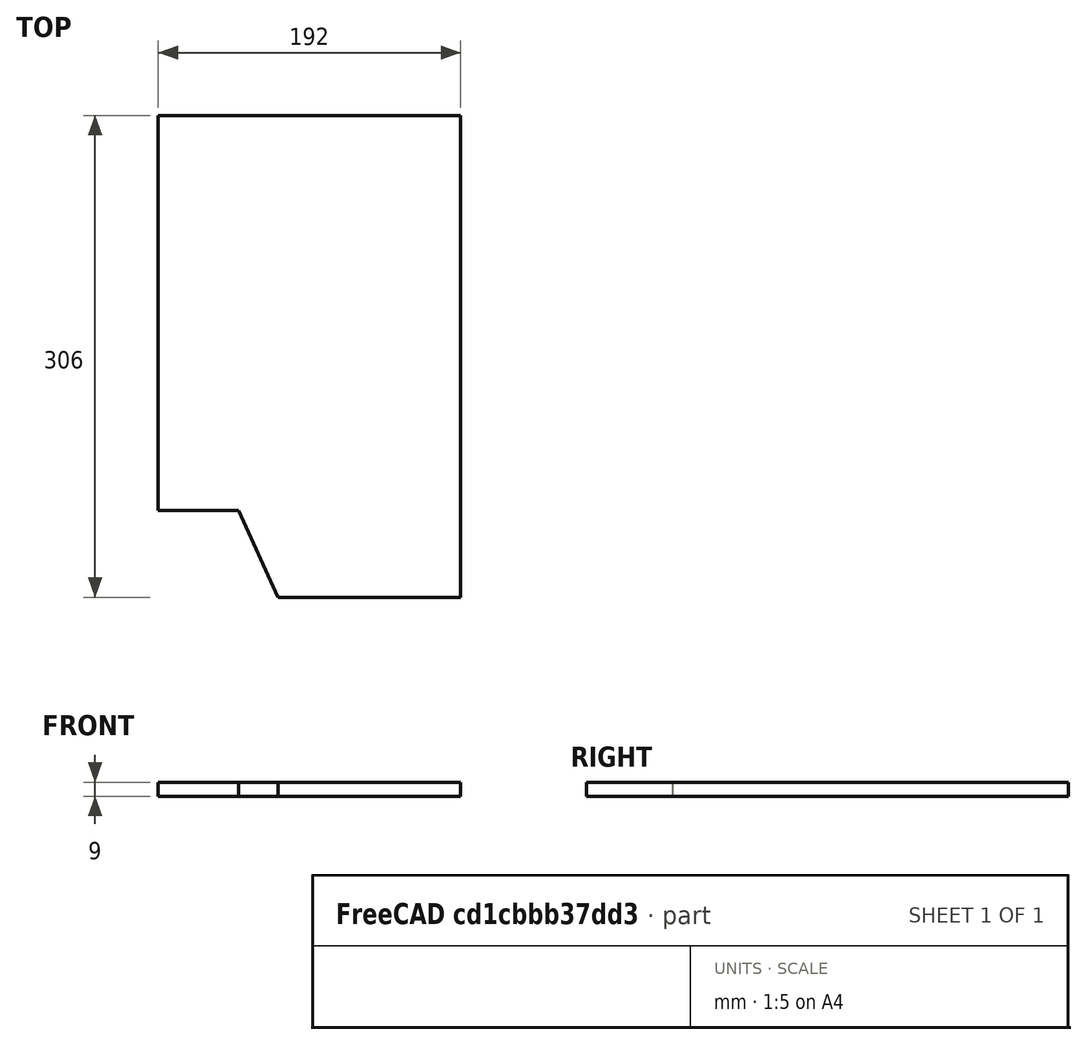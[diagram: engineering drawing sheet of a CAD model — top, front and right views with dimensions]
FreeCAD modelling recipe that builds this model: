
FCSTD DOCUMENT  (FreeCAD 0.16RUnknown)
Label: plaque_gd
License: All rights reserved
LicenseURL: http://en.wikipedia.org/wiki/All_rights_reserved
objects: App::FeaturePython×6, Drawing::FeatureViewPart×4, App::DocumentObjectGroup×4, Drawing::FeatureViewPython×3, Part::Plane×1, Part::Feature×1, Part::Cut×1, Part::FeaturePython×1, Part::Extrusion×1, Drawing::FeaturePage×1
note: 5 computed .brp shape members not serialized (recipe doc carries the construction recipe); baked Part::Feature solids carry a one-line shape summary decoded from their .brp

FEATURE [Part::Plane] square
  Length = 192
  Placement = pos=(9,20,0) rot=(0,0,1;0rad)
  Width = 306
FEATURE [Part::Feature] polygon
  shape: bbox 76 x 55 x 2e-07 mm, 1 faces, 0 solids (baked)
FEATURE [Part::Cut] difference
  Base = -> square
  Tool = -> polygon
FEATURE [Part::FeaturePython] RefineLinearExtrude  # WARN: FeaturePython — macro-defined, semantics opaque (R4)
  Base = -> difference
FEATURE [Part::Extrusion] LinearExtrude
  Base = -> RefineLinearExtrude
  Dir = (0,0,9)
  Solid = true
FEATURE [App::FeaturePython] Dimension001  # Draft dimension (typed FeaturePython)
  Dimline = (0,338,0)
  Direction = (0,0,0)
  Distance = 192
  End = (201,326,0)
  Normal = (0,0,1)
  Start = (9,326,0)
FEATURE [Drawing::FeatureViewPart] Ortho  label="Ortho_0_0"
  Direction = (1,0,0)
  HiddenWidth = 0.15
  LineWidth = 0.35
  Rotation = -90
  Scale = 0.38
  ShowHiddenLines = true
  ShowSmoothLines = false
  Source = -> LinearExtrude
  Tolerance = 0.05
  ViewResult = <g id="Ortho_0_0"\n   transform="rotate(-90,94.26,60.61) translate(94.26,60.61) scale(0.38,0.38)"\n  >\n<g   stroke="rgb(0, 0, 0)"\n   stroke-width="0.394737"\n   stroke-linecap="butt"\n   stroke-linejoin="miter"\n   stroke-dasharray="0.2,0.1"\n   fill="none"\n   transform="scale(1,-1)"\n  >\n<path id= "1" d=" M 0 -75 L 9 -75 " />\n<path id= "2" d=" M 0 -326 L 9 -326 " />\n<path id= "3" d=" M 0 -75 L 0 -326 " />\n<path id= "4" d=" M 9 -75 L 9 -326 " />\n<path id= "5" d=" M 0 -20 L 9 -20 " />\n<path id= "6" d=" M 0 -75 L 9 -75 " />\n<path id= "7" d=" M 0 -75 L 0 -20 " />\n<path id= "8" d=" M 9 -75 L 9 -20 " />\n</g>\n<g   stroke="rgb(0, 0, 0)"\n   stroke-width="0.921053"\n   stroke-linecap="butt"\n   stroke-linejoin="miter"\n   fill="none"\n   transform="scale(1,-1)"\n  >\n<path id= "1" d=" M 0 -326 L 9 -326 " />\n<path id= "2" d=" M 0 -20 L 9 -20 " />\n<path id= "3" d=" M 0 -20 L 0 -326 " />\n<path id= "4" d=" M 9 -20 L 9 -326 " />\n</g>\n</g>
  Visible = true
  X = 94.26
  Y = 60.61
FEATURE [Drawing::FeatureViewPart] Ortho001  label="Ortho_0_-1"
  Direction = (0,0,1)
  HiddenWidth = 0.15
  LineWidth = 0.35
  Rotation = 90
  Scale = 0.38
  ShowHiddenLines = false
  ShowSmoothLines = false
  Source = -> LinearExtrude
  Tolerance = 0.05
  ViewResult = <g id="Ortho_0_-1"\n   transform="rotate(90,94.26,103.89) translate(94.26,103.89) scale(0.38,0.38)"\n  >\n<g   stroke="rgb(0, 0, 0)"\n   stroke-width="0.921053"\n   stroke-linecap="butt"\n   stroke-linejoin="miter"\n   fill="none"\n   transform="scale(1,-1)"\n  >\n<path id= "1" d=" M 9 75 L 9 326 " />\n<path id= "2" d=" M 9 326 L 201 326 " />\n<path id= "3" d=" M 201 20 L 201 326 " />\n<path id= "4" d=" M 85 20 L 201 20 " />\n<path id= "5" d=" M 60 75 L 85 20 " />\n<path id= "6" d=" M 9 75 L 60 75 " />\n</g>\n</g>
  Visible = true
  X = 94.26
  Y = 103.89
FEATURE [Drawing::FeatureViewPart] Ortho002  label="Ortho_1_-1"
  Direction = (0.57735,-0.57735,0.57735)
  HiddenWidth = 0.15
  LineWidth = 0.35
  Rotation = 60
  Scale = 0.38
  ShowHiddenLines = false
  ShowSmoothLines = false
  Source = -> LinearExtrude
  Tolerance = 0.05
  ViewResult = <g id="Ortho_1_-1"\n   transform="rotate(60,238.99,155.737) translate(238.99,155.737) scale(0.38,0.38)"\n  >\n<g   stroke="rgb(0, 0, 0)"\n   stroke-width="0.921053"\n   stroke-linecap="butt"\n   stroke-linejoin="miter"\n   fill="none"\n   transform="scale(1,-1)"\n  >\n<path id= "1" d=" M 6.36396 64.9115 L 0 68.5857 " />\n<path id= "2" d=" M 0 68.5857 L 0 273.526 " />\n<path id= "3" d=" M 142.128 348.236 L 135.765 351.91 " />\n<path id= "4" d=" M 0 273.526 L 135.765 351.91 " />\n<path id= "5" d=" M 142.128 98.3878 L 135.765 102.062 " />\n<path id= "6" d=" M 142.128 98.3878 L 142.128 348.236 " />\n<path id= "7" d=" M 135.765 102.062 L 135.765 351.91 " />\n<path id= "8" d=" M 60.1041 51.031 L 53.7401 54.7053 " />\n<path id= "9" d=" M 60.1041 51.031 L 142.128 98.3878 " />\n<path id= "10" d=" M 53.7401 54.7053 L 135.765 102.062 " />\n<path id= "11" d=" M 36.0624 89.4064 L 53.7401 54.7053 " />\n<path id= "12" d=" M 6.36396 64.9115 L 38.9552 83.728 " />\n<path id= "13" d=" M 0 68.5857 L 36.0624 89.4064 " />\n</g>\n</g>
  Visible = true
  X = 238.99
  Y = 155.737
FEATURE [Drawing::FeatureViewPart] Ortho003  label="Ortho_-1_0"
  Direction = (0,1,0)
  HiddenWidth = 0.15
  LineWidth = 0.35
  Rotation = 180
  Scale = 0.38
  ShowHiddenLines = true
  ShowSmoothLines = false
  Source = -> LinearExtrude
  Tolerance = 0.05
  ViewResult = <g id="Ortho_-1_0"\n   transform="rotate(180,62.21,103.89) translate(62.21,103.89) scale(0.38,0.38)"\n  >\n<g   stroke="rgb(0, 0, 0)"\n   stroke-width="0.394737"\n   stroke-linecap="butt"\n   stroke-linejoin="miter"\n   stroke-dasharray="0.2,0.1"\n   fill="none"\n   transform="scale(1,-1)"\n  >\n<path id= "1" d=" M 0 9 L 9 9 " />\n<path id= "2" d=" M 0 201 L 9 201 " />\n<path id= "3" d=" M 0 85 L 9 85 " />\n<path id= "4" d=" M 0 85 L 0 201 " />\n<path id= "5" d=" M 9 85 L 9 201 " />\n<path id= "6" d=" M 0 60 L 9 60 " />\n<path id= "7" d=" M 0 60 L 0 85 " />\n<path id= "8" d=" M 9 60 L 9 85 " />\n<path id= "9" d=" M 0 9 L 0 60 " />\n<path id= "10" d=" M 9 9 L 9 60 " />\n</g>\n<g   stroke="rgb(0, 0, 0)"\n   stroke-width="0.921053"\n   stroke-linecap="butt"\n   stroke-linejoin="miter"\n   fill="none"\n   transform="scale(1,-1)"\n  >\n<path id= "1" d=" M 0 9 L 9 9 " />\n<path id= "2" d=" M 0 201 L 9 201 " />\n<path id= "3" d=" M 0 9 L 0 201 " />\n<path id= "4" d=" M 9 9 L 9 201 " />\n</g>\n</g>
  Visible = true
  X = 62.21
  Y = 103.89
FEATURE [App::FeaturePython] Dimension  # Draft dimension (typed FeaturePython)
  Dimline = (216,0,0)
  Direction = (0,0,0)
  Distance = 306
  End = (201,326,0)
  Normal = (0,0,1)
  Start = (201,20,0)
FEATURE [App::DocumentObjectGroup] Groupe001  label="XY"
  Group = -> [Dimension001,Dimension]
FEATURE [Drawing::FeatureViewPython] ViewGroupe001  # drawing view (typed FeaturePython)
  Direction = (0,0,1)
  FillStyle = 0
  FontSize = 12
  LineStyle = 0
  LineWidth = 0.35
  Rotation = 90
  Scale = 0.38
  Source = -> Groupe001
  ViewResult = <blob: 2026 chars omitted>
  Visible = true
  X = 94.26
  Y = 103.89
FEATURE [App::FeaturePython] Dimension008  # Draft dimension (typed FeaturePython)
  Dimline = (0,0,19)
  Direction = (0,0,0)
  Distance = 251
  End = (0,326,9)
  Normal = (-1,0,0)
  Start = (0,75,9)
FEATURE [App::FeaturePython] Dimension009  # Draft dimension (typed FeaturePython)
  Dimline = (0,0,19)
  Direction = (0,0,0)
  Distance = 55
  End = (0,75,9)
  Normal = (-1,0,0)
  Start = (0,20,9)
FEATURE [App::DocumentObjectGroup] Groupe002  label="YZ"
  Group = -> [Dimension008,Dimension009]
FEATURE [Drawing::FeatureViewPython] ViewGroupe002  # drawing view (typed FeaturePython)
  Direction = (1,0,0)
  FillStyle = 0
  FontSize = 12
  LineStyle = 0
  LineWidth = 0.35
  Rotation = -90
  Scale = 0.38
  Source = -> Groupe002
  ViewResult = <blob: 2017 chars omitted>
  Visible = true
  X = 94.26
  Y = 60.61
FEATURE [App::FeaturePython] Dimension010  # Draft dimension (typed FeaturePython)
  Dimline = (0,0,-10)
  Direction = (0,0,0)
  Distance = 25
  End = (85,0,0)
  Normal = (0,-1,-1.19209e-07)
  Start = (60,0,0)
FEATURE [App::FeaturePython] Dimension011  # Draft dimension (typed FeaturePython)
  Dimline = (0,0,25)
  Direction = (0,0,0)
  Distance = 51
  End = (60,0,9)
  Normal = (0,-1,-1.19209e-07)
  Start = (9,0,9)
FEATURE [App::DocumentObjectGroup] Groupe003  label="XZ"
  Group = -> [Dimension010,Dimension011]
FEATURE [App::DocumentObjectGroup] Groupe  label="Dimensions"
  Group = -> [Groupe001,Groupe002,Groupe003]
FEATURE [Drawing::FeatureViewPython] ViewGroupe003  # drawing view (typed FeaturePython)
  Direction = (0,1,0)
  FillStyle = 0
  FontSize = 12
  LineStyle = 0
  LineWidth = 0.35
  Rotation = 180
  Scale = 0.38
  Source = -> Groupe003
  ViewResult = <g id="ViewGroupe003" transform="rotate(180.0,62.21,103.89) translate(62.21,103.89) scale(0.38,-0.38)"><path d="M -0.0 60.0 L -10.0 60.0 L -10.0 85.0 L -0.0 85.0" fill="none" stroke="#000000" stroke-width="0.921052631579 px" style="stroke-width:0.921052631579;stroke-miterlimit:4;stroke-dasharray:none" freecad:basepoint1="-0.0 60.0" freecad:basepoint2="-0.0 85.0" freecad:dimpoint="-10.0 60.0"/>\n<path transform="rotate(90.0,-10.0,60.0) translate(-10.0,60.0) scale(0.666666666667,0.666666666667)" freecad:skip="1" fill="#000000" stroke="none" style="stroke-miterlimit:4;stroke-dasharray:none" d="M 0 0 L 4 1 L 4 -1 Z"/>\n<path transform="rotate(270.0,-10.0,85.0) translate(-10.0,85.0) scale(0.666666666667,0.666666666667)" freecad:skip="1" fill="#000000" stroke="none" style="stroke-miterlimit:4;stroke-dasharray:none" d="M 0 0 L 4 1 L 4 -1 Z"/>\n<text fill="#000000" font-size="15.7894736842" style="text-anchor:middle;text-align:center;font-family:" transform="rotate(90.0,-9.0,72.5) translate(-9.0,72.5) scale(1,-1) " freecad:skip="1">\n25,00 </text>\n<path d="M 9.0 9.0 L 25.0 9.0 L 25.0 60.0 L 9.0 60.0" fill="none" stroke="#000000" stroke-width="0.921052631579 px" style="stroke-width:0.921052631579;stroke-miterlimit:4;stroke-dasharray:none" freecad:basepoint1="9.0 9.0" freecad:basepoint2="9.0 60.0" freecad:dimpoint="25.0 9.0"/>\n<path transform="rotate(90.0,25.0,9.0) translate(25.0,9.0) scale(0.666666666667,0.666666666667)" freecad:skip="1" fill="#000000" stroke="none" style="stroke-miterlimit:4;stroke-dasharray:none" d="M 0 0 L 4 1 L 4 -1 Z"/>\n<path transform="rotate(270.0,25.0,60.0) translate(25.0,60.0) scale(0.666666666667,0.666666666667)" freecad:skip="1" fill="#000000" stroke="none" style="stroke-miterlimit:4;stroke-dasharray:none" d="M 0 0 L 4 1 L 4 -1 Z"/>\n<text fill="#000000" font-size="15.7894736842" style="text-anchor:middle;text-align:center;font-family:" transform="rotate(90.0,26.0,34.5) translate(26.0,34.5) scale(1,-1) " freecad:skip="1">\n51,00 </text>\n</g>
  Visible = true
  X = 62.21
  Y = 103.89
FEATURE [Drawing::FeaturePage] Page
  EditableTexts = AUTHOR NAME | CREATION DATE | SUPERVISOR NAME | CHECK DATE | 0,38 | WEIGHT | NUMBER | SHEET | Caisse | Plaque Gauche/Droite
  Group = -> [ViewGroupe001,Ortho,Ortho001,Ortho002,Ortho003,ViewGroupe002,ViewGroupe003]
